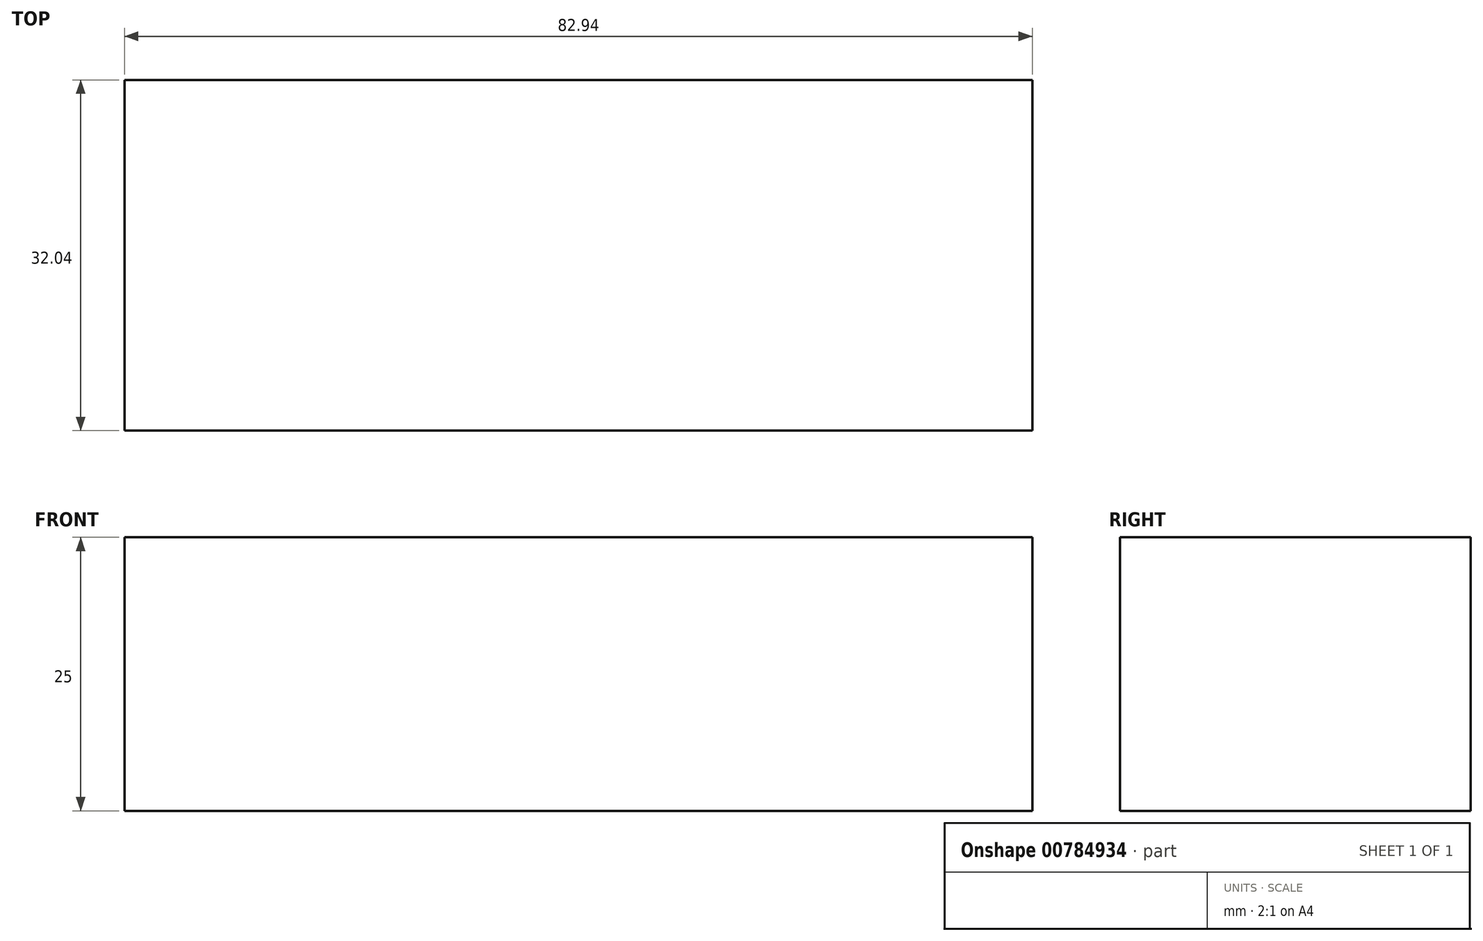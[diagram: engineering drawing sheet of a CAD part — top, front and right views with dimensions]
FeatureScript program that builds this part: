
annotation { "Feature Type Name" : "Feature", "Feature Type Description" : "" }
export const myFeature = defineFeature(function(context is Context, id is Id, definition is map)
    precondition{}
    {
        {
            var Q0;
            Q0=qCreatedBy(makeId("Top.planeOp"),FACE);
            var sketch = newSketch(context, id + "F0", { "sketchPlane" : qUnion([Q0])});
            skLineSegment(sketch, "E0.bottom", {"start": v(-41.47, 16.02) * mm, "end": v(41.47, 16.02) * mm});
            skLineSegment(sketch, "E0.top", {"start": v(-41.47, -16.02) * mm, "end": v(41.47, -16.02) * mm});
            skLineSegment(sketch, "E0.left", {"start": v(-41.47, 16.02) * mm, "end": v(-41.47, -16.02) * mm});
            skLineSegment(sketch, "E0.right", {"start": v(41.47, 16.02) * mm, "end": v(41.47, -16.02) * mm});
            skPoint(sketch, "E0.middle", {"position": v(0, 0) * mm});
            skSolve(sketch);
        }
        {
            var Q0;
            Q0=qSketchRegion(id+"F0",true);
            extrude(context, id + "F1", {"entities" : qUnion([Q0]), "depth" : 25 * mm, "offsetDistance" : 25 * mm});
        }
    });
